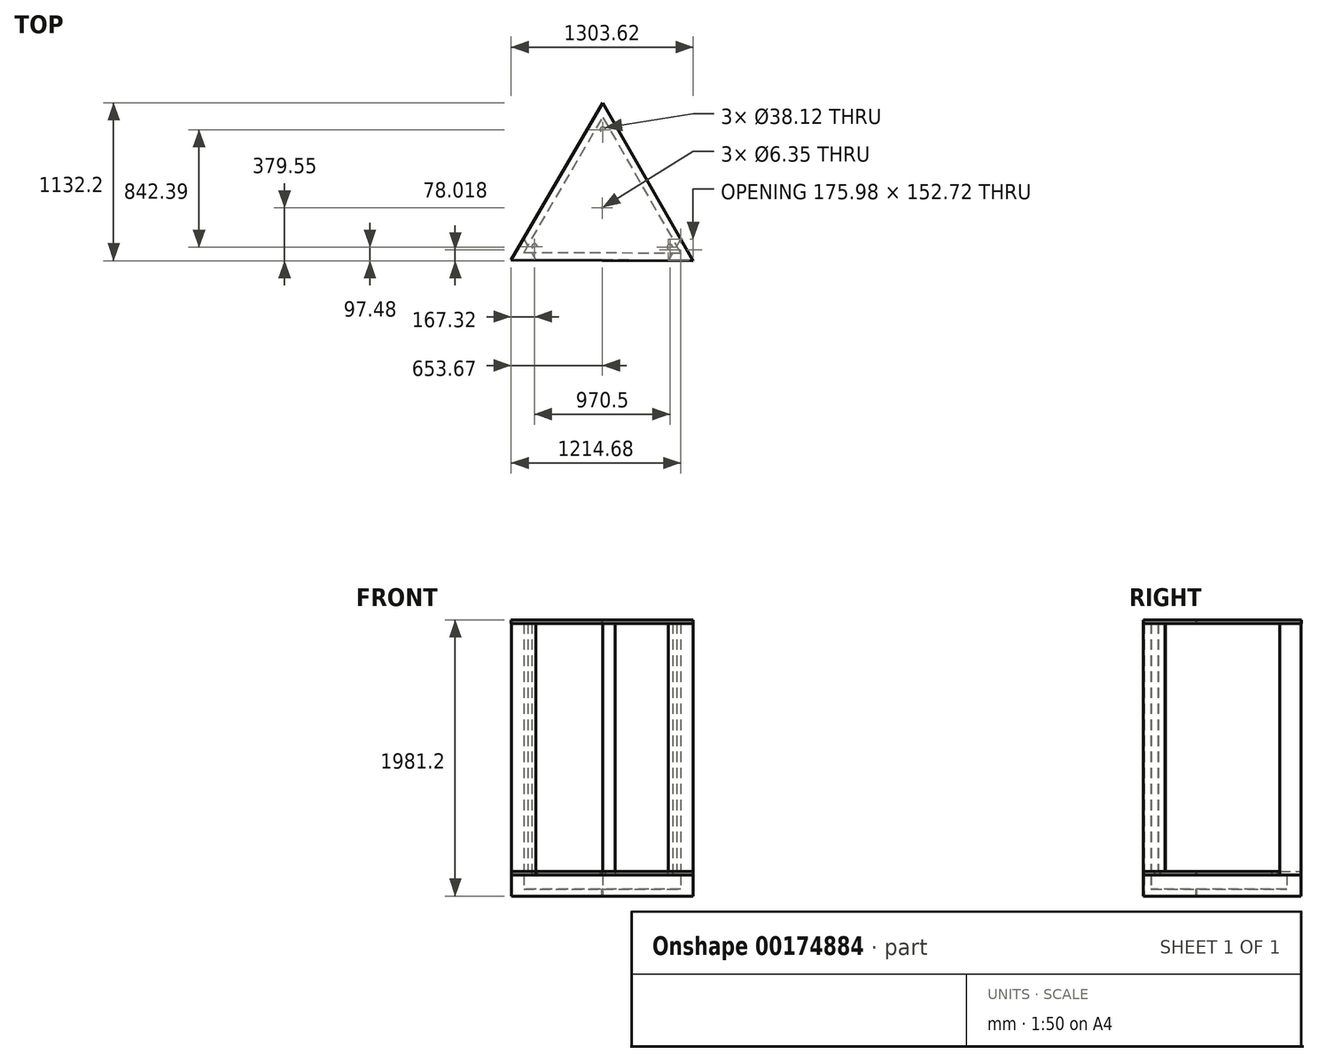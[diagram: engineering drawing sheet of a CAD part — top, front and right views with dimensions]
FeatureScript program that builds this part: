
annotation { "Feature Type Name" : "Feature", "Feature Type Description" : "" }
export const myFeature = defineFeature(function(context is Context, id is Id, definition is map)
    precondition{}
    {
        {
            var Q0;
            Q0=qCreatedBy(makeId("Top.planeOp"),FACE);
            var sketch = newSketch(context, id + "F0", { "sketchPlane" : qUnion([Q0])});
            skCircle(sketch, "E0.cCircle", {"center": v(0, 0) * mm, "radius": 324.7 * mm, "construction": true});
            skLineSegment(sketch, "E0.0", {"start": v(2.4, 649.4) * mm, "end": v(561.2, -326.77) * mm});
            skLineSegment(sketch, "E0.1", {"start": v(561.2, -326.77) * mm, "end": v(-563.59, -322.63) * mm});
            skLineSegment(sketch, "E0.2", {"start": v(-563.59, -322.63) * mm, "end": v(2.4, 649.4) * mm});
            skPoint(sketch, "E0.0.midPoint", {"position": v(281.8, 161.31) * mm});
            skSolve(sketch);
        }
        {
            var Q0;
            Q0=makeQuery(id+"F0.imprint","IMPRINT",FACE,{"disambiguationData":[TD([[makeQuery(id+"F0.imprint","IMPRINT",EDGE,{"derivedFrom":sQuery(id+"F0.wireOp",EDGE,"E0.0")}),-1.0]])]});
            extrude(context, id + "F1", {"entities" : qUnion([Q0]), "depth" : 101.6 * mm});
        }
        {
            var Q0;
            Q0=makeQuery(id+"F1.opExtrude","CAP_FACE",FACE,{"disambiguationData":[OSD([sQuery(id+"F0.wireOp",EDGE,"E0.0"),sQuery(id+"F0.wireOp",EDGE,"E0.1"),sQuery(id+"F0.wireOp",EDGE,"E0.2")])],"isStart":false});
            shell(context, id + "F2", {"entities" : qUnion([Q0]), "thickness" : 50.8 * mm, "oppositeDirection" : true});
        }
        {
            var Q0;
            Q0=makeQuery(id+"F1.opExtrude","CAP_FACE",FACE,{"disambiguationData":[OSD([sQuery(id+"F0.wireOp",EDGE,"E0.0"),sQuery(id+"F0.wireOp",EDGE,"E0.1"),sQuery(id+"F0.wireOp",EDGE,"E0.2")])],"isStart":false});
            var sketch = newSketch(context, id + "F3", { "sketchPlane" : qUnion([Q0])});
            skCircle(sketch, "E1.cCircle", {"center": v(0, 0) * mm, "radius": 375.5 * mm, "construction": true});
            skLineSegment(sketch, "E1.0", {"start": v(2.77, 751) * mm, "end": v(649, -377.9) * mm});
            skLineSegment(sketch, "E1.1", {"start": v(649, -377.9) * mm, "end": v(-651.76, -373.1) * mm});
            skLineSegment(sketch, "E1.2", {"start": v(-651.76, -373.1) * mm, "end": v(2.77, 751) * mm});
            skPoint(sketch, "E1.0.midPoint", {"position": v(325.88, 186.55) * mm});
            skCircle(sketch, "E2.cCircle", {"center": v(561.2, -326.77) * mm, "radius": 50.8 * mm, "construction": true});
            skLineSegment(sketch, "E2.0", {"start": v(561.57, -225.17) * mm, "end": v(649, -377.9) * mm});
            skLineSegment(sketch, "E2.1", {"start": v(649, -377.9) * mm, "end": v(473.02, -377.24) * mm});
            skLineSegment(sketch, "E2.2", {"start": v(473.02, -377.24) * mm, "end": v(561.57, -225.17) * mm});
            skPoint(sketch, "E2.0.midPoint", {"position": v(605.28, -301.53) * mm});
            skCircle(sketch, "E3.1.0", {"center": v(2.4, 649.4) * mm, "radius": 50.8 * mm, "construction": true});
            skCircle(sketch, "E3.2.0", {"center": v(-563.59, -322.63) * mm, "radius": 50.8 * mm, "construction": true});
            skLineSegment(sketch, "E4.1.0", {"start": v(2.77, 751) * mm, "end": v(90.2, 598.27) * mm});
            skLineSegment(sketch, "E4.1.2", {"start": v(90.2, 598.27) * mm, "end": v(-85.78, 598.92) * mm});
            skLineSegment(sketch, "E4.1.3", {"start": v(-85.78, 598.92) * mm, "end": v(2.77, 751) * mm});
            skLineSegment(sketch, "E4.2.0", {"start": v(-651.76, -373.1) * mm, "end": v(-563.21, -221.03) * mm});
            skLineSegment(sketch, "E4.2.2", {"start": v(-563.21, -221.03) * mm, "end": v(-475.79, -373.75) * mm});
            skLineSegment(sketch, "E4.2.3", {"start": v(-475.79, -373.75) * mm, "end": v(-651.76, -373.1) * mm});
            skPoint(sketch, "E5", {"position": v(2.2, 560.32) * mm});
            skPoint(sketch, "E5.positionSnap0", {"position": v(2.2, 598.6) * mm});
            skPoint(sketch, "E6.1.0", {"position": v(-486.35, -278.25) * mm});
            skPoint(sketch, "E6.2.0", {"position": v(484.15, -282.07) * mm});
            skCircle(sketch, "E7", {"center": v(2.2, 560.32) * mm, "radius": 19.06 * mm});
            skCircle(sketch, "E8.1.0", {"center": v(-486.35, -278.25) * mm, "radius": 19.06 * mm});
            skCircle(sketch, "E8.2.0", {"center": v(484.15, -282.07) * mm, "radius": 19.06 * mm});
            skSolve(sketch);
        }
        {
            var Q0;
            Q0=qSketchRegion(id+"F3",true);
            extrude(context, id + "F4", {"entities" : qUnion([Q0]), "operationType" : NewBodyOperationType.ADD, "depth" : 25.4 * mm});
        }
        {
            var Q0;
            {var subQ1=sQuery(id+"F3.wireOp",EDGE,"E2.0");Q0=makeQuery(id+"F3.imprint","IMPRINT",FACE,{"disambiguationData":[TD([[makeQuery(id+"F3.imprint","IMPRINT",EDGE,{"derivedFrom":subQ1}),-1.0]])]});}
            var Q1;
            {var subQ5=sQuery(id+"F3.wireOp",EDGE,"E4.2.0");Q1=makeQuery(id+"F3.imprint","IMPRINT",FACE,{"disambiguationData":[TD([[makeQuery(id+"F3.imprint","IMPRINT",EDGE,{"derivedFrom":subQ5}),-1.0]])]});}
            var Q2;
            {var subQ5=sQuery(id+"F3.wireOp",EDGE,"E4.1.0");Q2=makeQuery(id+"F3.imprint","IMPRINT",FACE,{"disambiguationData":[TD([[makeQuery(id+"F3.imprint","IMPRINT",EDGE,{"derivedFrom":subQ5}),-1.0]])]});}
            extrude(context, id + "F5", {"entities" : qUnion([Q0, Q1, Q2]), "operationType" : NewBodyOperationType.ADD, "depth" : 1828.8 * mm});
        }
        {
            var Q0;
            Q0=makeQuery(id+"F5.opExtrude","CAP_FACE",FACE,{"disambiguationData":[OSD([sQuery(id+"F0.wireOp",EDGE,"E0.0"),sQuery(id+"F0.wireOp",EDGE,"E0.2"),sQuery(id+"F3.wireOp",EDGE,"E4.1.0"),sQuery(id+"F3.wireOp",EDGE,"E4.1.2"),sQuery(id+"F3.wireOp",EDGE,"E4.1.3")])],"isStart":false});
            var sketch = newSketch(context, id + "F6", { "sketchPlane" : qUnion([Q0])});
            skCircle(sketch, "E9.cCircle", {"center": v(0, 0) * mm, "radius": 376.33 * mm, "construction": true});
            skLineSegment(sketch, "E9.0", {"start": v(3.72, 752.65) * mm, "end": v(649.95, -379.55) * mm});
            skLineSegment(sketch, "E9.1", {"start": v(649.95, -379.55) * mm, "end": v(-653.67, -373.1) * mm});
            skLineSegment(sketch, "E9.2", {"start": v(-653.67, -373.1) * mm, "end": v(3.72, 752.65) * mm});
            skPoint(sketch, "E9.0.midPoint", {"position": v(326.84, 186.55) * mm});
            skSolve(sketch);
        }
        {
            var Q0;
            Q0=makeQuery(id+"F6.imprint","IMPRINT",FACE,{"disambiguationData":[TD([[makeQuery(id+"F6.imprint","IMPRINT",EDGE,{"derivedFrom":sQuery(id+"F6.wireOp",EDGE,"E9.0")}),-1.0]])]});
            extrude(context, id + "F7", {"entities" : qUnion([Q0]), "operationType" : NewBodyOperationType.ADD, "oppositeDirection" : true, "depth" : 25.4 * mm});
        }
        {
            var Q0;
            Q0=sQuery(id+"F6.wireOp",VERTEX,"E9.cCircle.center");
            var Q1;
            Q1=makeQuery(id+"F1.opExtrude","SWEPT_BODY",BODY,{"disambiguationData":[OSD([sQuery(id+"F0.wireOp",EDGE,"E0.0"),sQuery(id+"F0.wireOp",EDGE,"E0.1"),sQuery(id+"F0.wireOp",EDGE,"E0.2")])]});
            hole(context, id + "F8", {"style" : HoleStyle.SIMPLE, "endStyle" : HoleEndStyle.THROUGH, "holeDiameter" : 6.35 * mm, "locations" : qUnion([Q0]), "scope" : qUnion([Q1]), "isTappedThrough" : true});
        }
    });
